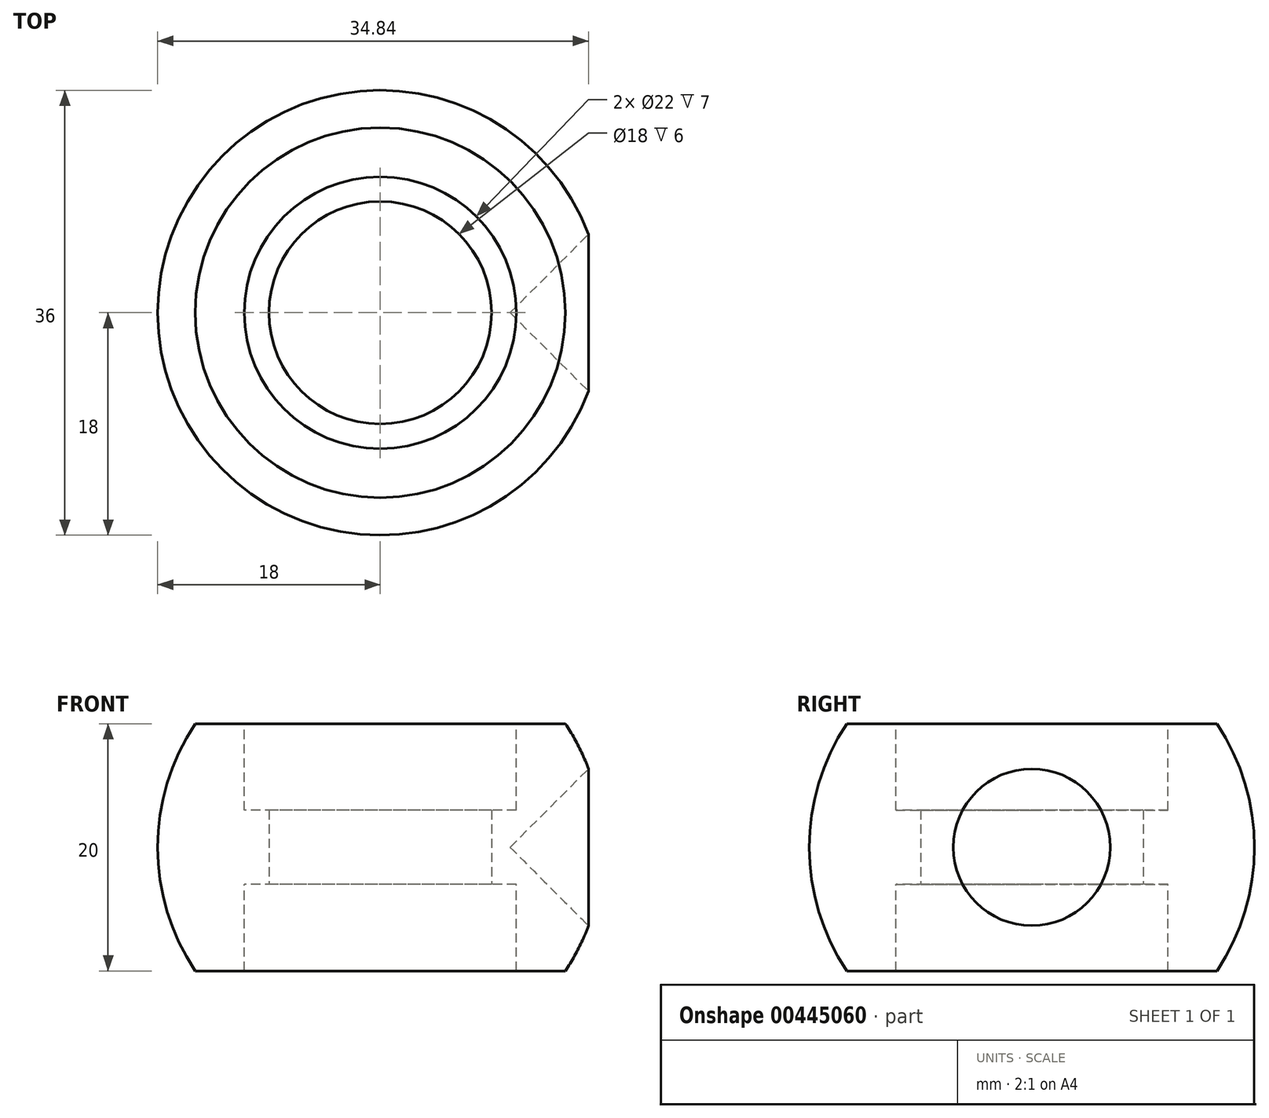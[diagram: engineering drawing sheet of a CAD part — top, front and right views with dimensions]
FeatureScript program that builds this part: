
annotation { "Feature Type Name" : "Feature", "Feature Type Description" : "" }
export const myFeature = defineFeature(function(context is Context, id is Id, definition is map)
    precondition{}
    {
        {
            var Q0;
            Q0=qCreatedBy(makeId("Front.planeOp"),FACE);
            var sketch = newSketch(context, id + "F0", { "sketchPlane" : qUnion([Q0])});
            skArc(sketch, "E0", {"start": v(14.97, 10) * mm, "mid": v(18, 0) * mm, "end": v(14.97, -10) * mm});
            skLineSegment(sketch, "E1", {"start": v(0, 10) * mm, "end": v(14.97, 10) * mm});
            skLineSegment(sketch, "E2", {"start": v(0, -10) * mm, "end": v(14.97, -10) * mm});
            skLineSegment(sketch, "E3", {"start": v(14.97, 10) * mm, "end": v(14.97, -10) * mm});
            skPoint(sketch, "E4", {"position": v(14.97, 0) * mm});
            skLineSegment(sketch, "E5", {"start": v(0, 10) * mm, "end": v(0, -10) * mm});
            skSolve(sketch);
        }
        {
            var Q0;
            Q0=qSketchRegion(id+"F0",true);
            var Q1;
            Q1=sQuery(id+"F0.wireOp",EDGE,"E5");
            revolve(context, id + "F1", {"entities" : qUnion([Q0]), "axis" : qUnion([Q1]), "revolveType" : RevolveType.FULL});
        }
        {
            var Q0;
            Q0=qCreatedBy(makeId("Top.planeOp"),FACE);
            var sketch = newSketch(context, id + "F2", { "sketchPlane" : qUnion([Q0])});
            skLineSegment(sketch, "E6", {"start": v(30.5, 0) * mm, "end": v(39.5, -9) * mm});
            skLineSegment(sketch, "E7", {"start": v(39.5, -9) * mm, "end": v(39.5, 9) * mm});
            skLineSegment(sketch, "E8", {"start": v(39.5, 9) * mm, "end": v(30.5, 0) * mm});
            skLineSegment(sketch, "E9", {"start": v(39.5, 0) * mm, "end": v(30.5, 0) * mm});
            skSolve(sketch);
        }
        {
            var Q0;
            {var subQ0=sQuery(id+"F2.wireOp",EDGE,"E8");Q0=makeQuery(id+"F2.imprint","IMPRINT",FACE,{"disambiguationData":[TD([[makeQuery(id+"F2.imprint","IMPRINT",EDGE,{"derivedFrom":subQ0}),1.0]])]});}
            var Q1;
            Q1=sQuery(id+"F2.wireOp",EDGE,"E9");
            revolve(context, id + "F3", {"operationType" : NewBodyOperationType.REMOVE, "entities" : qUnion([Q0]), "axis" : qUnion([Q1]), "revolveType" : RevolveType.FULL, "oppositeDirection" : true});
        }
        {
            var Q0;
            Q0=makeQuery(id+"F1.opRevolve","SWEPT_FACE",FACE,{"disambiguationData":[OSD([sQuery(id+"F0.wireOp",EDGE,"E1")])]});
            var sketch = newSketch(context, id + "F4", { "sketchPlane" : qUnion([Q0])});
            skCircle(sketch, "E10", {"center": v(0, 0) * mm, "radius": 11 * mm});
            skSolve(sketch);
        }
        {
            var Q0;
            Q0 = qSketchRegion(id + "F4", true);
            extrude(context, id + "F5", {"entities" : qUnion([Q0]), "operationType" : NewBodyOperationType.REMOVE, "endBound" : BoundingType.THROUGH_ALL, "oppositeDirection" : true, "depth" : 25 * mm});
        }
        {
            var Q0;
            Q0=qCreatedBy(makeId("Top.planeOp"),FACE);
            var sketch = newSketch(context, id + "F6", { "sketchPlane" : qUnion([Q0])});
            skCircle(sketch, "E11.0", {"center": v(0, 0) * mm, "radius": 9 * mm});
            skCircle(sketch, "E12.0", {"center": v(0, 0) * mm, "radius": 12 * mm});
            skSolve(sketch);
        }
        {
            var Q0;
            Q0 = qSketchRegion(id + "F6", true);
            extrude(context, id + "F7", {"entities" : qUnion([Q0]), "operationType" : NewBodyOperationType.ADD, "endBound" : BoundingType.SYMMETRIC, "depth" : 6 * mm});
        }
        {
            var Q0;
            Q0=qCreatedBy(makeId("Front.planeOp"),FACE);
            var sketch = newSketch(context, id + "F8", { "sketchPlane" : qUnion([Q0])});
            skLineSegment(sketch, "E13", {"start": v(10.5, 0) * mm, "end": v(19.5, -9) * mm});
            skLineSegment(sketch, "E14", {"start": v(19.5, -9) * mm, "end": v(19.5, 9) * mm});
            skLineSegment(sketch, "E15", {"start": v(19.5, 9) * mm, "end": v(10.5, 0) * mm});
            skLineSegment(sketch, "E16", {"start": v(19.5, 0) * mm, "end": v(10.5, 0) * mm});
            skSolve(sketch);
        }
        {
            var Q0;
            {var subQ0=sQuery(id+"F8.wireOp",EDGE,"E15");Q0=makeQuery(id+"F8.imprint","IMPRINT",FACE,{"disambiguationData":[TD([[makeQuery(id+"F8.imprint","IMPRINT",EDGE,{"derivedFrom":subQ0}),1.0]])]});}
            var Q1;
            Q1=sQuery(id+"F8.wireOp",EDGE,"E16");
            revolve(context, id + "F9", {"operationType" : NewBodyOperationType.REMOVE, "entities" : qUnion([Q0]), "axis" : qUnion([Q1]), "revolveType" : RevolveType.FULL, "oppositeDirection" : true});
        }
    });
